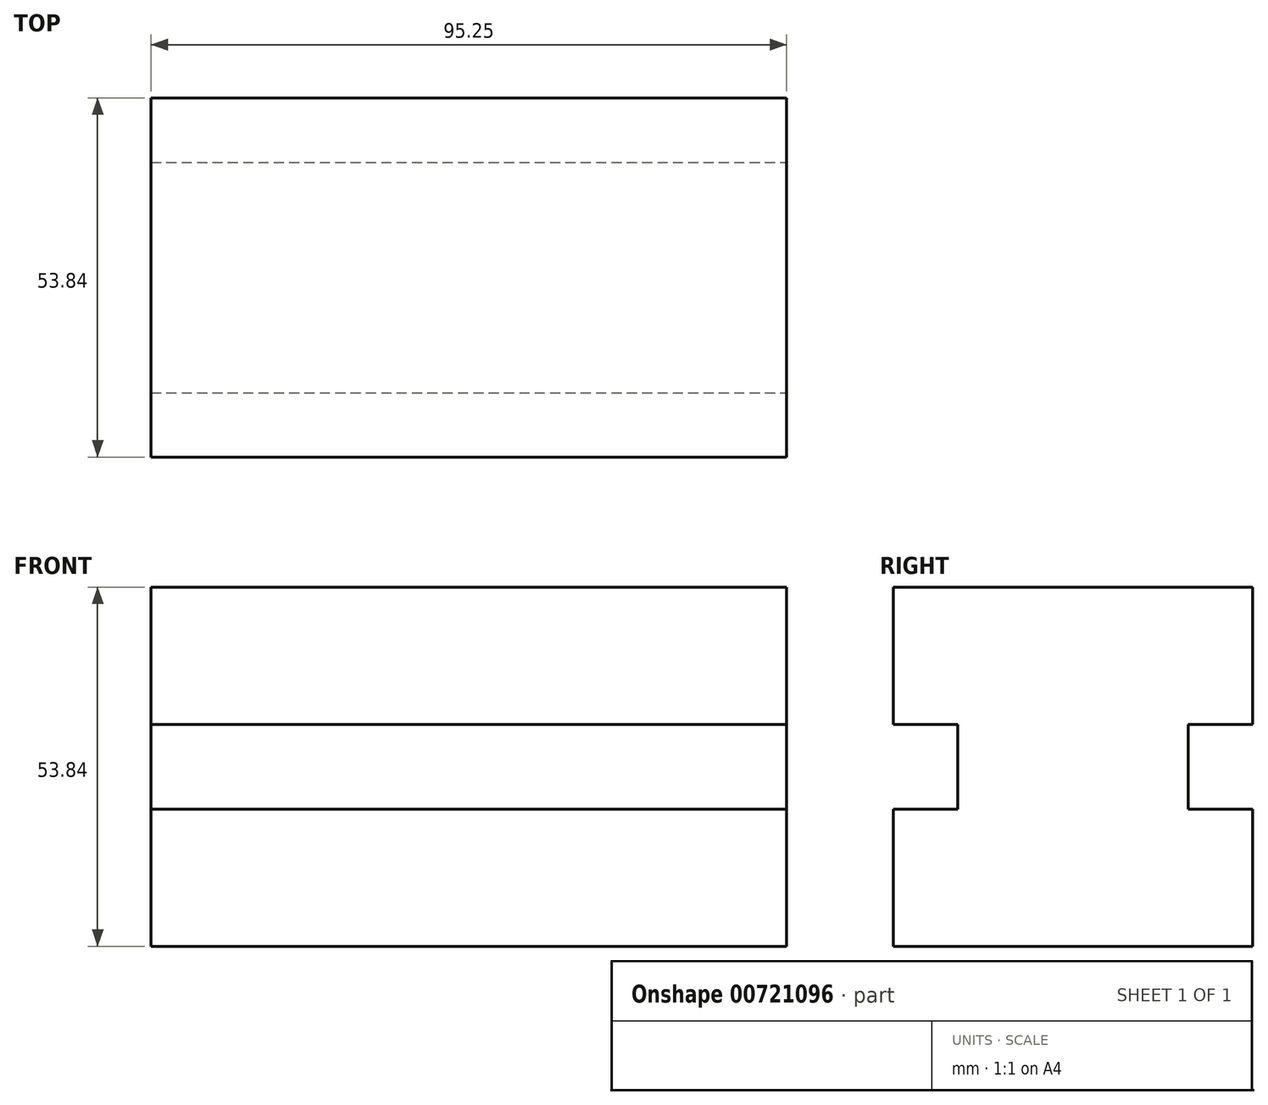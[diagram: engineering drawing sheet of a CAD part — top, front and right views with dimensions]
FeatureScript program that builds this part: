
annotation { "Feature Type Name" : "Feature", "Feature Type Description" : "" }
export const myFeature = defineFeature(function(context is Context, id is Id, definition is map)
    precondition{}
    {
        {
            var Q0;
            Q0=qCreatedBy(makeId("Right.planeOp"),FACE);
            var sketch = newSketch(context, id + "F0", { "sketchPlane" : qUnion([Q0])});
            skLineSegment(sketch, "E0.bottom", {"start": v(26.92, -26.92) * mm, "end": v(-26.92, -26.92) * mm});
            skLineSegment(sketch, "E0.top", {"start": v(26.92, 26.92) * mm, "end": v(-26.92, 26.92) * mm});
            skLineSegment(sketch, "E0.left", {"start": v(26.92, -26.92) * mm, "end": v(26.92, -6.35) * mm});
            skLineSegment(sketch, "E0.right", {"start": v(-26.92, -26.92) * mm, "end": v(-26.92, -6.35) * mm});
            skPoint(sketch, "E0.middle", {"position": v(0, 0) * mm});
            skLineSegment(sketch, "E1.bottom", {"start": v(-26.92, 6.35) * mm, "end": v(-17.27, 6.35) * mm});
            skLineSegment(sketch, "E1.top", {"start": v(-26.92, -6.35) * mm, "end": v(-17.27, -6.35) * mm});
            skLineSegment(sketch, "E1.right", {"start": v(-17.27, 6.35) * mm, "end": v(-17.27, -6.35) * mm});
            skLineSegment(sketch, "E2", {"start": v(0, 30.12) * mm, "end": v(0, -69.26) * mm, "construction": true});
            skLineSegment(sketch, "E3.MirrorCS", {"start": v(26.92, 6.35) * mm, "end": v(17.27, 6.35) * mm});
            skLineSegment(sketch, "E4.MirrorCS", {"start": v(17.27, 6.35) * mm, "end": v(17.27, -6.35) * mm});
            skLineSegment(sketch, "E5.MirrorCS", {"start": v(26.92, -6.35) * mm, "end": v(17.27, -6.35) * mm});
            skLineSegment(sketch, "E6.trimOffspring", {"start": v(-26.92, 6.35) * mm, "end": v(-26.92, 26.92) * mm});
            skLineSegment(sketch, "E7.trimOffspring", {"start": v(26.92, 6.35) * mm, "end": v(26.92, 26.92) * mm});
            skSolve(sketch);
        }
        {
            var Q0;
            Q0=makeQuery(id+"F0.imprint","IMPRINT",FACE,{"disambiguationData":[TD([[makeQuery(id+"F0.imprint","IMPRINT",EDGE,{"derivedFrom":sQuery(id+"F0.wireOp",EDGE,"E0.bottom")}),-1.0]])]});
            extrude(context, id + "F1", {"entities" : qUnion([Q0]), "oppositeDirection" : true, "depth" : 95.25 * mm, "offsetDistance" : 25.4 * mm});
        }
    });
